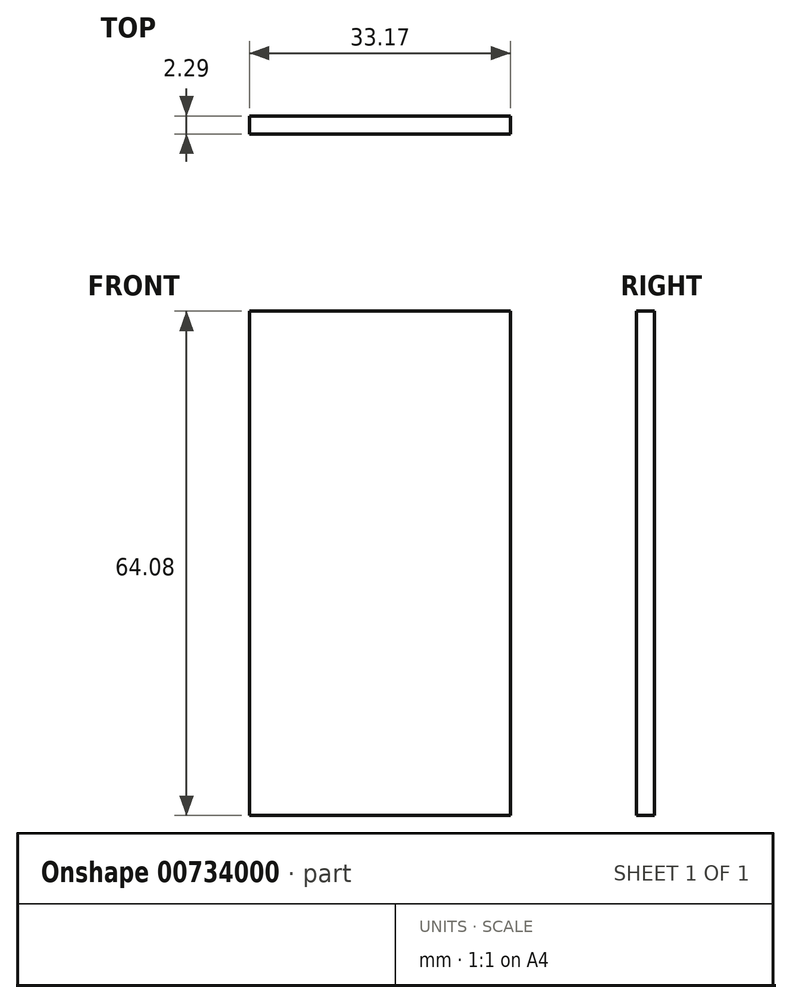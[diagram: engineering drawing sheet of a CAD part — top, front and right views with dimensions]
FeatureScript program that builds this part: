
annotation { "Feature Type Name" : "Feature", "Feature Type Description" : "" }
export const myFeature = defineFeature(function(context is Context, id is Id, definition is map)
    precondition{}
    {
        {
            var Q0;
            Q0=qCreatedBy(makeId("Front.planeOp"),FACE);
            var sketch = newSketch(context, id + "F0", { "sketchPlane" : qUnion([Q0])});
            skLineSegment(sketch, "E0.bottom", {"start": v(-16.8, 32.04) * mm, "end": v(16.36, 32.04) * mm});
            skLineSegment(sketch, "E0.top", {"start": v(-16.8, -32.04) * mm, "end": v(16.36, -32.04) * mm});
            skLineSegment(sketch, "E0.left", {"start": v(-16.8, 32.04) * mm, "end": v(-16.8, -32.04) * mm});
            skLineSegment(sketch, "E0.right", {"start": v(16.36, 32.04) * mm, "end": v(16.36, -32.04) * mm});
            skSolve(sketch);
        }
        {
            var Q0;
            Q0=makeQuery(id+"F0.imprint","IMPRINT",FACE,{"disambiguationData":[TD([[makeQuery(id+"F0.imprint","IMPRINT",EDGE,{"derivedFrom":sQuery(id+"F0.wireOp",EDGE,"E0.bottom")}),-1.0]])]});
            extrude(context, id + "F1", {"entities" : qUnion([Q0]), "depth" : 2.3 * mm, "offsetDistance" : 25.4 * mm});
        }
    });
